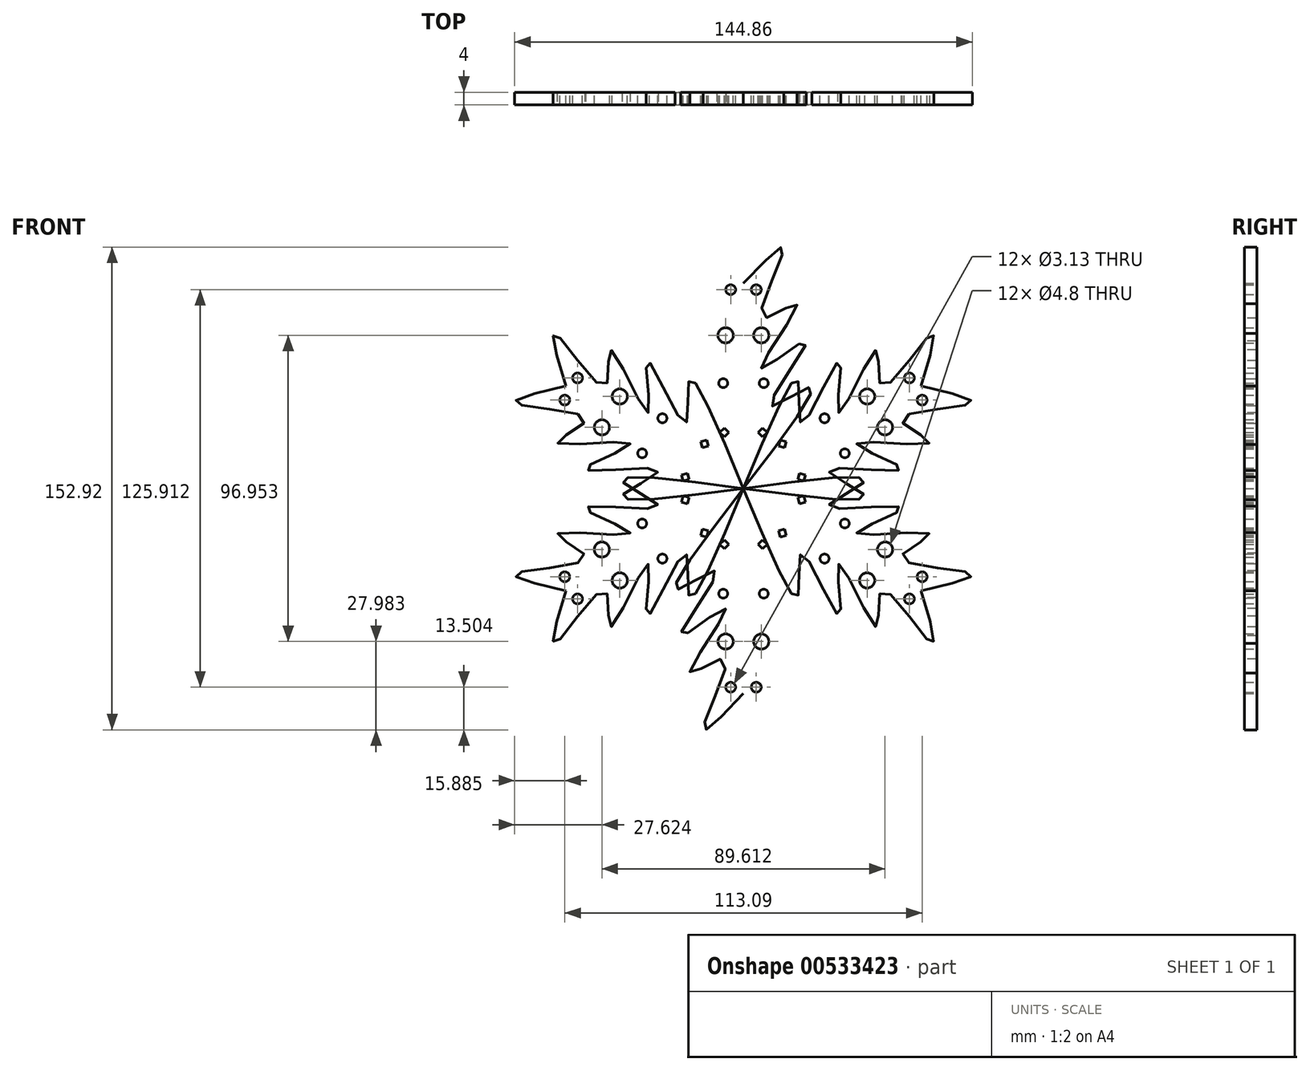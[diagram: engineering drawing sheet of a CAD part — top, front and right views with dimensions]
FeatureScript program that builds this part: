
annotation { "Feature Type Name" : "Feature", "Feature Type Description" : "" }
export const myFeature = defineFeature(function(context is Context, id is Id, definition is map)
    precondition{}
    {
        {
            var Q0;
            Q0=qCreatedBy(makeId("Front.planeOp"),FACE);
            var sketch = newSketch(context, id + "F0", { "sketchPlane" : qUnion([Q0])});
            skLineSegment(sketch, "E0", {"start": v(0, 0) * mm, "end": v(0, 64.95) * mm, "construction": true});
            skFitSpline(sketch, "E1", {"points": [v(0, 64.95) * mm, v(12.7, 75.77) * mm, v(6.12, 54.12) * mm, v(16.94, 58.36) * mm, v(5.65, 38.12) * mm, v(19.77, 46.6) * mm, v(8.47, 26.36) * mm, v(20.7, 32) * mm, v(0, 0) * mm], "startDerivative": vector(169.18, 180.51) * mm, "endDerivative": vector(-220.4, -286.94) * mm});
            skCircle(sketch, "E2", {"center": v(5.65, 48.48) * mm, "radius": 2.4 * mm});
            skCircle(sketch, "E3", {"center": v(4.05, 62.96) * mm, "radius": 1.57 * mm});
            skLineSegment(sketch, "E4.bottom", {"start": v(6.08, 19.15) * mm, "end": v(7.5, 17.74) * mm});
            skLineSegment(sketch, "E4.top", {"start": v(4.67, 17.74) * mm, "end": v(6.08, 16.32) * mm});
            skLineSegment(sketch, "E4.left", {"start": v(6.08, 19.15) * mm, "end": v(4.67, 17.74) * mm});
            skLineSegment(sketch, "E4.right", {"start": v(7.5, 17.74) * mm, "end": v(6.08, 16.32) * mm});
            skCircle(sketch, "E5", {"center": v(6.41, 33.33) * mm, "radius": 1.43 * mm});
            skLineSegment(sketch, "E6.MirrorCS", {"start": v(-6.08, 19.15) * mm, "end": v(-4.67, 17.74) * mm});
            skLineSegment(sketch, "E7.MirrorCS", {"start": v(-7.5, 17.74) * mm, "end": v(-6.08, 16.32) * mm});
            skLineSegment(sketch, "E8.MirrorCS", {"start": v(-6.08, 19.15) * mm, "end": v(-7.5, 17.74) * mm});
            skLineSegment(sketch, "E9.MirrorCS", {"start": v(-4.67, 17.74) * mm, "end": v(-6.08, 16.32) * mm});
            skCircle(sketch, "E10.MirrorC", {"center": v(-4.05, 62.96) * mm, "radius": 1.57 * mm});
            skCircle(sketch, "E11.MirrorC", {"center": v(-6.41, 33.33) * mm, "radius": 1.43 * mm});
            skCircle(sketch, "E12.MirrorC", {"center": v(-5.65, 48.48) * mm, "radius": 2.4 * mm});
            skFitSpline(sketch, "E13.MirrorCS", {"points": [v(0, 64.95) * mm, v(-12.7, 75.77) * mm, v(-6.12, 54.12) * mm, v(-16.94, 58.36) * mm, v(-5.65, 38.12) * mm, v(-19.77, 46.6) * mm, v(-8.47, 26.36) * mm, v(-20.7, 32) * mm, v(0, 0) * mm], "startDerivative": vector(-169.18, 180.51) * mm, "endDerivative": vector(220.4, -286.94) * mm});
            skSolve(sketch);
        }
        {
            var Q0;
            Q0 = qSketchRegion(id + "F0", true);
            extrude(context, id + "F1", {"entities" : qUnion([Q0]), "depth" : 4 * mm, "offsetDistance" : 25.4 * mm});
        }
        {
            var Q0;
            Q0=qCreatedBy(makeId("Right.planeOp"),FACE);
            var sketch = newSketch(context, id + "F2", { "sketchPlane" : qUnion([Q0])});
            skLineSegment(sketch, "E14", {"start": v(0, 0) * mm, "end": v(-68.83, 0) * mm, "construction": true});
            skSolve(sketch);
        }
        {
            var Q0;
            Q0=makeQuery(id+"F1.opExtrude","SWEPT_BODY",BODY,{"disambiguationData":[OSD([sQuery(id+"F0.wireOp",EDGE,"E1"),sQuery(id+"F0.wireOp",EDGE,"E2"),sQuery(id+"F0.wireOp",EDGE,"E3"),sQuery(id+"F0.wireOp",EDGE,"E4.bottom"),sQuery(id+"F0.wireOp",EDGE,"E4.top"),sQuery(id+"F0.wireOp",EDGE,"E4.left"),sQuery(id+"F0.wireOp",EDGE,"E4.right"),sQuery(id+"F0.wireOp",EDGE,"E5"),sQuery(id+"F0.wireOp",EDGE,"E6.MirrorCS"),sQuery(id+"F0.wireOp",EDGE,"E7.MirrorCS"),sQuery(id+"F0.wireOp",EDGE,"E8.MirrorCS"),sQuery(id+"F0.wireOp",EDGE,"E9.MirrorCS"),sQuery(id+"F0.wireOp",EDGE,"E10.MirrorC"),sQuery(id+"F0.wireOp",EDGE,"E11.MirrorC"),sQuery(id+"F0.wireOp",EDGE,"E12.MirrorC"),sQuery(id+"F0.wireOp",EDGE,"E13.MirrorCS")])]});
            var Q1;
            Q1=sQuery(id+"F2.wireOp",EDGE,"E14");
            circularPattern(context, id + "F3", {"entities" : qUnion([Q0]), "axis" : qUnion([Q1]), "angle" : 360 * degree, "instanceCount" : 6, "equalSpace" : true});
        }
    });
